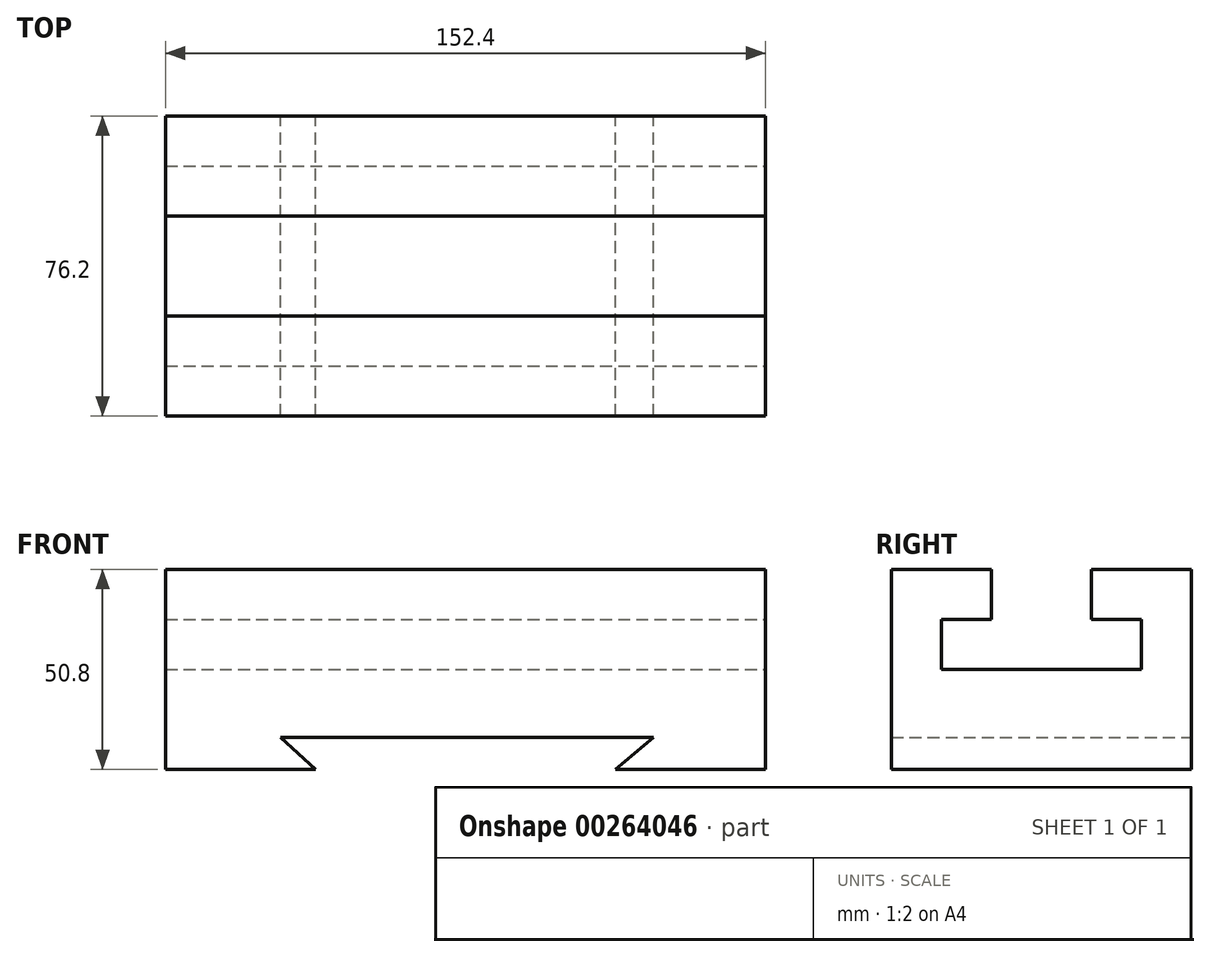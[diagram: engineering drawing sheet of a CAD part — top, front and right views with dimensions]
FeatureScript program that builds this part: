
annotation { "Feature Type Name" : "Feature", "Feature Type Description" : "" }
export const myFeature = defineFeature(function(context is Context, id is Id, definition is map)
    precondition{}
    {
        {
            var Q0;
            Q0=qCreatedBy(makeId("Front.planeOp"),FACE);
            var sketch = newSketch(context, id + "F0", { "sketchPlane" : qUnion([Q0])});
            skLineSegment(sketch, "E0.bottom", {"start": v(-82.13, 50.8) * mm, "end": v(70.27, 50.8) * mm});
            skLineSegment(sketch, "E0.left", {"start": v(-82.13, 50.8) * mm, "end": v(-82.13, 12.7) * mm});
            skLineSegment(sketch, "E0.right", {"start": v(70.27, 50.8) * mm, "end": v(70.27, 12.7) * mm});
            skLineSegment(sketch, "E1", {"start": v(-82.13, 12.7) * mm, "end": v(-82.13, 0) * mm});
            skLineSegment(sketch, "E2", {"start": v(70.27, 12.7) * mm, "end": v(70.27, 0) * mm});
            skLineSegment(sketch, "E3", {"start": v(70.27, 0) * mm, "end": v(32.17, 0) * mm});
            skLineSegment(sketch, "E4", {"start": v(-82.13, 0) * mm, "end": v(-44.03, 0) * mm});
            skLineSegment(sketch, "E5", {"start": v(-57.14, 8.2) * mm, "end": v(44.46, 8.2) * mm});
            skLineSegment(sketch, "E6", {"start": v(32.17, 0) * mm, "end": v(41.87, 8.2) * mm});
            skLineSegment(sketch, "E7", {"start": v(-44.03, 0) * mm, "end": v(-52.96, 8.2) * mm});
            skSolve(sketch);
        }
        {
            var Q0;
            Q0 = qSketchRegion(id + "F0", true);
            extrude(context, id + "F1", {"entities" : qUnion([Q0]), "depth" : 12.7 * mm});
        }
        {
            var Q0;
            Q0=makeQuery(id+"F1.opExtrude","CAP_FACE",FACE,{"disambiguationData":[OSD([sQuery(id+"F0.wireOp",EDGE,"E0.bottom"),sQuery(id+"F0.wireOp",EDGE,"E0.left"),sQuery(id+"F0.wireOp",EDGE,"E0.right"),sQuery(id+"F0.wireOp",EDGE,"E1"),sQuery(id+"F0.wireOp",EDGE,"E2"),sQuery(id+"F0.wireOp",EDGE,"E3"),sQuery(id+"F0.wireOp",EDGE,"E4"),sQuery(id+"F0.wireOp",EDGE,"E5"),sQuery(id+"F0.wireOp",EDGE,"E6"),sQuery(id+"F0.wireOp",EDGE,"E7")])],"isStart":false});
            extrude(context, id + "F2", {"entities" : qUnion([Q0]), "operationType" : NewBodyOperationType.ADD, "depth" : 63.5 * mm});
        }
        {
            var Q0;
            {var subQ0=sQuery(id+"F0.wireOp",EDGE,"E2");var subQ1=sQuery(id+"F0.wireOp",EDGE,"E0.right");Q0=makeQuery(id+"F2.boolean.opBoolean","MERGE",FACE,{"derivedFrom":[makeQuery(id+"F1.opExtrude","SWEPT_FACE",FACE,{"disambiguationData":[OSD([subQ1,subQ0])]}),makeQuery(id+"F2.opExtrude","SWEPT_FACE",FACE,{"disambiguationData":[OSD([subQ1,subQ0])]})]});}
            var sketch = newSketch(context, id + "F3", { "sketchPlane" : qUnion([Q0])});
            skLineSegment(sketch, "E8", {"start": v(-76.2, 50.8) * mm, "end": v(-50.8, 50.8) * mm});
            skLineSegment(sketch, "E9", {"start": v(0, 50.8) * mm, "end": v(-25.4, 50.8) * mm});
            skLineSegment(sketch, "E10", {"start": v(-25.4, 50.8) * mm, "end": v(-25.4, 38.1) * mm});
            skLineSegment(sketch, "E11", {"start": v(-50.8, 50.8) * mm, "end": v(-50.8, 38.1) * mm});
            skLineSegment(sketch, "E12", {"start": v(-25.4, 38.1) * mm, "end": v(-12.7, 38.1) * mm});
            skLineSegment(sketch, "E13", {"start": v(-50.8, 38.1) * mm, "end": v(-63.5, 38.1) * mm});
            skLineSegment(sketch, "E14", {"start": v(-63.5, 38.1) * mm, "end": v(-63.5, 25.39) * mm});
            skLineSegment(sketch, "E15", {"start": v(-12.7, 38.1) * mm, "end": v(-12.7, 25.4) * mm});
            skLineSegment(sketch, "E16", {"start": v(-63.5, 25.39) * mm, "end": v(-12.7, 25.4) * mm});
            skSolve(sketch);
        }
        {
            var Q0;
            {var subQ1=sQuery(id+"F3.wireOp",EDGE,"E10");Q0=makeQuery(id+"F3.imprint","IMPRINT",FACE,{"disambiguationData":[TD([[makeQuery(id+"F3.imprint","IMPRINT",EDGE,{"derivedFrom":subQ1}),-1.0]])]});}
            extrude(context, id + "F4", {"entities" : qUnion([Q0]), "operationType" : NewBodyOperationType.REMOVE, "endBound" : BoundingType.UP_TO_NEXT, "oppositeDirection" : true, "depth" : 25.4 * mm});
        }
    });
